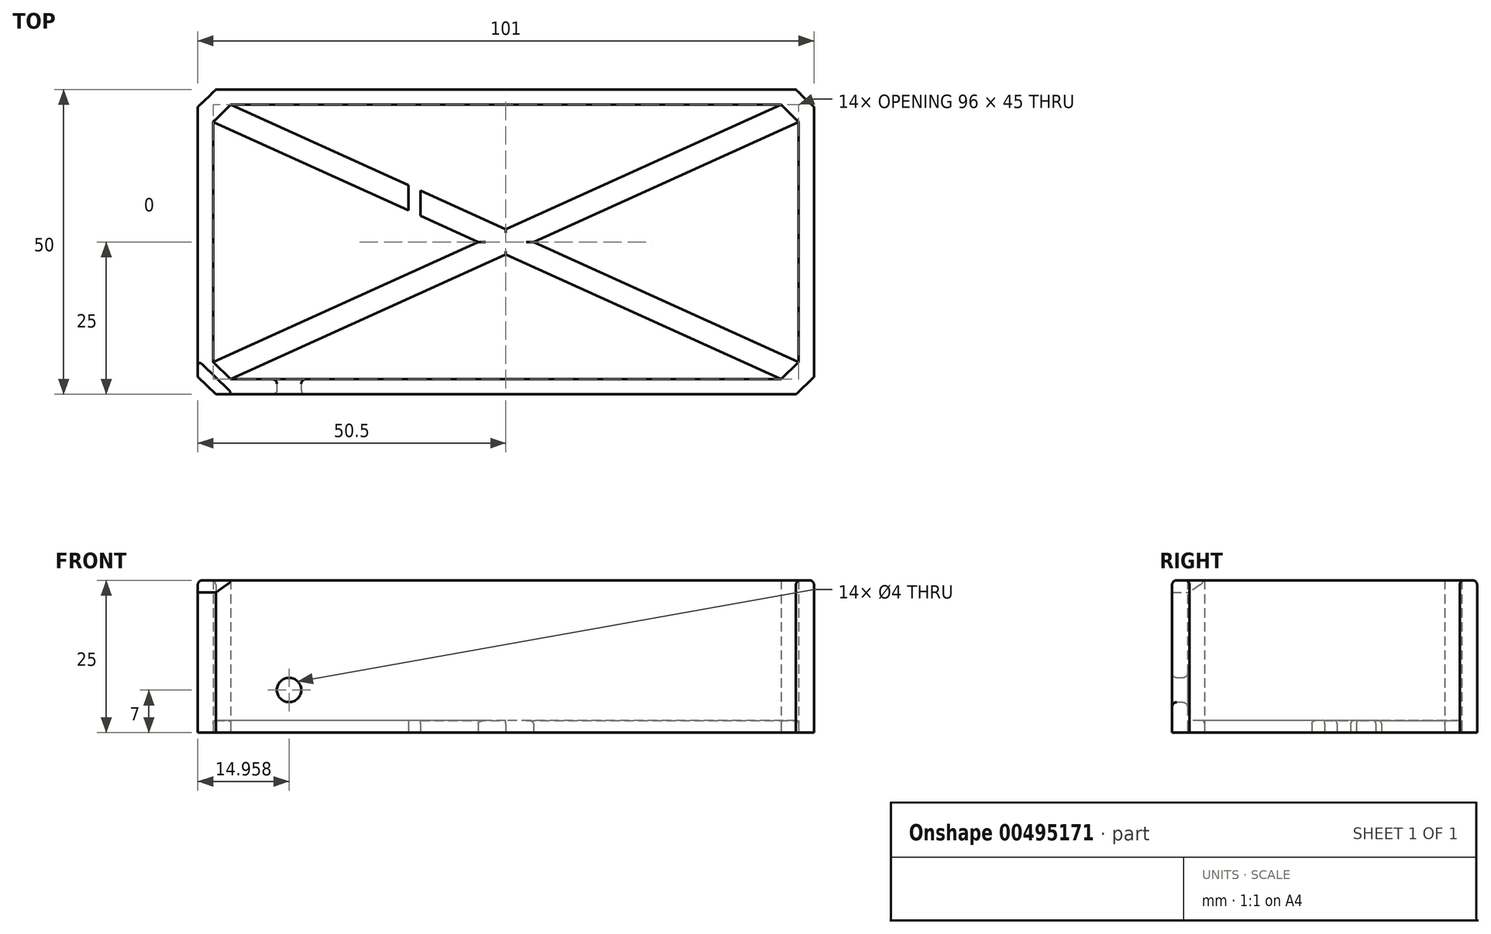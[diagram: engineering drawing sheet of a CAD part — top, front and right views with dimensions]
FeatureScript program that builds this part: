
annotation { "Feature Type Name" : "Feature", "Feature Type Description" : "" }
export const myFeature = defineFeature(function(context is Context, id is Id, definition is map)
    precondition{}
    {
        {
            var Q0;
            Q0=qCreatedBy(makeId("Top.planeOp"),FACE);
            var sketch = newSketch(context, id + "F0", { "sketchPlane" : qUnion([Q0])});
            skLineSegment(sketch, "E0.bottom", {"start": v(-47.54, 25) * mm, "end": v(47.54, 25) * mm});
            skLineSegment(sketch, "E0.top", {"start": v(-47.54, -25) * mm, "end": v(47.54, -25) * mm});
            skLineSegment(sketch, "E0.left", {"start": v(-50.5, 22.14) * mm, "end": v(-50.5, -22.14) * mm});
            skLineSegment(sketch, "E0.right", {"start": v(50.5, 22.14) * mm, "end": v(50.5, -22.14) * mm});
            skPoint(sketch, "E0.middle", {"position": v(0, 0) * mm});
            skLineSegment(sketch, "E1", {"start": v(-47.54, 25) * mm, "end": v(-50.5, 22.14) * mm});
            skPoint(sketch, "E2.orphan", {"position": v(-50.5, 25) * mm});
            skLineSegment(sketch, "E3.MirrorCS", {"start": v(-47.54, -25) * mm, "end": v(-50.5, -22.14) * mm});
            skLineSegment(sketch, "E4.MirrorCS", {"start": v(47.54, 25) * mm, "end": v(50.5, 22.14) * mm});
            skLineSegment(sketch, "E5.MirrorCS", {"start": v(47.54, -25) * mm, "end": v(50.5, -22.14) * mm});
            skPoint(sketch, "E6.orphan", {"position": v(50.5, 25) * mm});
            skPoint(sketch, "E7.orphan", {"position": v(50.5, -25) * mm});
            skPoint(sketch, "E8.orphan", {"position": v(-50.5, -25) * mm});
            skLineSegment(sketch, "E9.bottom", {"start": v(-45.1, 22.5) * mm, "end": v(45.1, 22.5) * mm});
            skLineSegment(sketch, "E9.top", {"start": v(-45.1, -22.5) * mm, "end": v(45.1, -22.5) * mm});
            skLineSegment(sketch, "E9.left", {"start": v(-48, 19.7) * mm, "end": v(-48, -19.7) * mm});
            skLineSegment(sketch, "E9.right", {"start": v(48, 19.7) * mm, "end": v(48, -19.7) * mm});
            skLineSegment(sketch, "E10", {"start": v(-48, -19.7) * mm, "end": v(-45.1, -22.5) * mm});
            skPoint(sketch, "E11.orphan", {"position": v(-48, -22.5) * mm});
            skLineSegment(sketch, "E12.MirrorCS", {"start": v(-48, 19.7) * mm, "end": v(-45.1, 22.5) * mm});
            skPoint(sketch, "E13.orphan", {"position": v(-48, 22.5) * mm});
            skLineSegment(sketch, "E14.MirrorCS", {"start": v(48, 19.7) * mm, "end": v(45.1, 22.5) * mm});
            skLineSegment(sketch, "E15.MirrorCS", {"start": v(48, -19.7) * mm, "end": v(45.1, -22.5) * mm});
            skPoint(sketch, "E16.orphan", {"position": v(48, 22.5) * mm});
            skPoint(sketch, "E17.orphan", {"position": v(48, -22.5) * mm});
            skLineSegment(sketch, "E18", {"start": v(-14, 8.4) * mm, "end": v(0, 2.06) * mm});
            skLineSegment(sketch, "E19", {"start": v(45.1, -22.5) * mm, "end": v(0, -2.06) * mm});
            skLineSegment(sketch, "E20", {"start": v(45.1, 22.5) * mm, "end": v(0, 2.06) * mm});
            skLineSegment(sketch, "E21", {"start": v(48, 19.7) * mm, "end": v(4.55, 0) * mm});
            skLineSegment(sketch, "E22.trimOffspring", {"start": v(-4.55, 0) * mm, "end": v(-14, 4.28) * mm});
            skLineSegment(sketch, "E23.trimOffspring", {"start": v(-4.55, 0) * mm, "end": v(-48, -19.7) * mm});
            skLineSegment(sketch, "E24.trimOffspring", {"start": v(4.55, 0) * mm, "end": v(48, -19.7) * mm});
            skLineSegment(sketch, "E25.trimOffspring", {"start": v(0, -2.06) * mm, "end": v(-45.1, -22.5) * mm});
            skLineSegment(sketch, "E26.bottom", {"start": v(-45.1, 22.5) * mm, "end": v(-14, 22.5) * mm});
            skLineSegment(sketch, "E26.top", {"start": v(-48, 1.5) * mm, "end": v(-14, 1.5) * mm});
            skLineSegment(sketch, "E26.left", {"start": v(-48, 19.7) * mm, "end": v(-48, 1.5) * mm});
            skLineSegment(sketch, "E26.right", {"start": v(-14, 22.5) * mm, "end": v(-14, 8.4) * mm});
            skLineSegment(sketch, "E27", {"start": v(-16, 5.19) * mm, "end": v(-48, 19.7) * mm});
            skLineSegment(sketch, "E28", {"start": v(-16, 9.31) * mm, "end": v(-45.1, 22.5) * mm});
            skLineSegment(sketch, "E29.bottom", {"start": v(-45.1, 22.5) * mm, "end": v(-16, 22.5) * mm});
            skLineSegment(sketch, "E29.top", {"start": v(-48, 3.5) * mm, "end": v(-16, 3.5) * mm});
            skLineSegment(sketch, "E29.left", {"start": v(-48, 19.7) * mm, "end": v(-48, 3.5) * mm});
            skLineSegment(sketch, "E29.right", {"start": v(-16, 22.5) * mm, "end": v(-16, 9.31) * mm});
            skLineSegment(sketch, "E30.trimOffspring", {"start": v(-16, 5.19) * mm, "end": v(-16, 3.5) * mm});
            skLineSegment(sketch, "E31.trimOffspring", {"start": v(-14, 4.28) * mm, "end": v(-14, 1.5) * mm});
            skLineSegment(sketch, "E32", {"start": v(-16, 9.31) * mm, "end": v(-16, 5.19) * mm});
            skLineSegment(sketch, "E33", {"start": v(-14, 8.4) * mm, "end": v(-14, 4.28) * mm});
            skSolve(sketch);
        }
        {
            var Q0;
            Q0=makeQuery(id+"F0.imprint","IMPRINT",FACE,{"disambiguationData":[TD([[makeQuery(id+"F0.imprint","IMPRINT",EDGE,{"derivedFrom":sQuery(id+"F0.wireOp",EDGE,"E0.bottom")}),-1.0]])]});
            extrude(context, id + "F1", {"entities" : qUnion([Q0]), "depth" : 25 * mm});
        }
        {
            var Q0;
            Q0=makeQuery(id+"F1.opExtrude","SWEPT_FACE",FACE,{"disambiguationData":[OSD([sQuery(id+"F0.wireOp",EDGE,"E0.top")])]});
            var sketch = newSketch(context, id + "F2", { "sketchPlane" : qUnion([Q0])});
            skCircle(sketch, "E34", {"center": v(-35.54, 7) * mm, "radius": 2 * mm});
            skPoint(sketch, "E34.first.point", {"position": v(-37.5, 7.44) * mm});
            skPoint(sketch, "E34.second.point", {"position": v(-33.55, 6.79) * mm});
            skPoint(sketch, "E34.third.point", {"position": v(-36.16, 5.1) * mm});
            skSolve(sketch);
        }
        {
            var Q0;
            Q0=makeQuery(id+"F2.imprint","IMPRINT",FACE,{"disambiguationData":[TD([[makeQuery(id+"F2.imprint","IMPRINT",EDGE,{"derivedFrom":sQuery(id+"F2.wireOp",EDGE,"E34")}),1.0]])]});
            extrude(context, id + "F3", {"entities" : qUnion([Q0]), "operationType" : NewBodyOperationType.REMOVE, "oppositeDirection" : true, "depth" : 25 * mm});
        }
        {
            var Q0;
            Q0=makeQuery(id+"F1.opExtrude","CAP_EDGE",EDGE,{"disambiguationData":[OSD([sQuery(id+"F0.wireOp",EDGE,"E3.MirrorCS")])],"isStart":false});
            var Q1;
            Q1=makeQuery(id+"F1.opExtrude","CAP_EDGE",EDGE,{"disambiguationData":[OSD([sQuery(id+"F0.wireOp",EDGE,"E5.MirrorCS")])],"isStart":false});
            var Q2;
            Q2=makeQuery(id+"F1.opExtrude","CAP_EDGE",EDGE,{"disambiguationData":[OSD([sQuery(id+"F0.wireOp",EDGE,"E4.MirrorCS")])],"isStart":false});
            var Q3;
            Q3=makeQuery(id+"F1.opExtrude","CAP_EDGE",EDGE,{"disambiguationData":[OSD([sQuery(id+"F0.wireOp",EDGE,"E1")])],"isStart":false});
            chamfer(context, id + "F4", {"entities" : qUnion([Q0, Q1, Q2, Q3]), "width" : 2 * mm, "tangentPropagation" : true});
        }
        {
            var Q0;
            Q0=makeQuery(id+"F0.imprint","IMPRINT",FACE,{"disambiguationData":[TD([[makeQuery(id+"F0.imprint","IMPRINT",EDGE,{"derivedFrom":sQuery(id+"F0.wireOp",EDGE,"E12.MirrorCS")}),-1.0]])]});
            var Q1;
            Q1=makeQuery(id+"F0.imprint","IMPRINT",FACE,{"disambiguationData":[TD([[makeQuery(id+"F0.imprint","IMPRINT",EDGE,{"derivedFrom":sQuery(id+"F0.wireOp",EDGE,"E26.bottom")}),-1.0]])]});
            var Q2;
            Q2=makeQuery(id+"F0.imprint","IMPRINT",FACE,{"disambiguationData":[TD([[makeQuery(id+"F0.imprint","IMPRINT",EDGE,{"derivedFrom":sQuery(id+"F0.wireOp",EDGE,"E10")}),1.0]])]});
            extrude(context, id + "F5", {"entities" : qUnion([Q0, Q1, Q2]), "depth" : 2 * mm});
        }
        {
            var Q0;
            Q0=makeQuery(id+"F5.opExtrude","CAP_EDGE",EDGE,{"disambiguationData":[OSD([sQuery(id+"F0.wireOp",EDGE,"E28")])],"isStart":false});
            var Q1;
            Q1=makeQuery(id+"F5.opExtrude","CAP_EDGE",EDGE,{"disambiguationData":[OSD([sQuery(id+"F0.wireOp",EDGE,"E27")])],"isStart":false});
            var Q2;
            Q2=makeQuery(id+"F5.opExtrude","CAP_EDGE",EDGE,{"disambiguationData":[OSD([sQuery(id+"F0.wireOp",EDGE,"E29.top")])],"isStart":false});
            var Q3;
            Q3=makeQuery(id+"F5.opExtrude","CAP_EDGE",EDGE,{"disambiguationData":[OSD([sQuery(id+"F0.wireOp",EDGE,"E26.top")])],"isStart":false});
            var Q4;
            Q4=makeQuery(id+"F5.opExtrude","CAP_EDGE",EDGE,{"disambiguationData":[OSD([sQuery(id+"F0.wireOp",EDGE,"E31.trimOffspring")])],"isStart":false});
            var Q5;
            Q5=makeQuery(id+"F5.opExtrude","CAP_EDGE",EDGE,{"disambiguationData":[OSD([sQuery(id+"F0.wireOp",EDGE,"E22.trimOffspring")])],"isStart":false});
            var Q6;
            Q6=makeQuery(id+"F5.opExtrude","CAP_EDGE",EDGE,{"disambiguationData":[OSD([sQuery(id+"F0.wireOp",EDGE,"E20")])],"isStart":false});
            var Q7;
            Q7=makeQuery(id+"F5.opExtrude","CAP_EDGE",EDGE,{"disambiguationData":[OSD([sQuery(id+"F0.wireOp",EDGE,"E21")])],"isStart":false});
            var Q8;
            Q8=makeQuery(id+"F5.opExtrude","CAP_EDGE",EDGE,{"disambiguationData":[OSD([sQuery(id+"F0.wireOp",EDGE,"E19")])],"isStart":false});
            var Q9;
            Q9=makeQuery(id+"F5.opExtrude","CAP_EDGE",EDGE,{"disambiguationData":[OSD([sQuery(id+"F0.wireOp",EDGE,"E24.trimOffspring")])],"isStart":false});
            var Q10;
            Q10=makeQuery(id+"F5.opExtrude","CAP_EDGE",EDGE,{"disambiguationData":[OSD([sQuery(id+"F0.wireOp",EDGE,"E25.trimOffspring")])],"isStart":false});
            var Q11;
            Q11=makeQuery(id+"F5.opExtrude","CAP_EDGE",EDGE,{"disambiguationData":[OSD([sQuery(id+"F0.wireOp",EDGE,"E23.trimOffspring")])],"isStart":false});
            var Q12;
            Q12=makeQuery(id+"F5.opExtrude","CAP_EDGE",EDGE,{"disambiguationData":[OSD([sQuery(id+"F0.wireOp",EDGE,"E26.right")])],"isStart":false});
            var Q13;
            Q13=makeQuery(id+"F5.opExtrude","CAP_EDGE",EDGE,{"disambiguationData":[OSD([sQuery(id+"F0.wireOp",EDGE,"E29.right")])],"isStart":false});
            var Q14;
            Q14=makeQuery(id+"F5.opExtrude","CAP_EDGE",EDGE,{"disambiguationData":[OSD([sQuery(id+"F0.wireOp",EDGE,"E18")])],"isStart":false});
            fillet(context, id + "F6", {"entities" : qUnion([Q0, Q1, Q2, Q3, Q4, Q5, Q6, Q7, Q8, Q9, Q10, Q11, Q12, Q13, Q14]), "radius" : .5 * mm, "tangentPropagation" : true, "allowEdgeOverflow" : false});
        }
        {
            var Q0;
            Q0=makeQuery(id+"F1.opExtrude","CAP_EDGE",EDGE,{"disambiguationData":[OSD([sQuery(id+"F0.wireOp",EDGE,"E0.top")])],"isStart":false});
            var Q1;
            Q1=makeQuery(id+"F1.opExtrude","CAP_EDGE",EDGE,{"disambiguationData":[OSD([sQuery(id+"F0.wireOp",EDGE,"E0.left")])],"isStart":false});
            var Q2;
            Q2=makeQuery(id+"F1.opExtrude","CAP_EDGE",EDGE,{"disambiguationData":[OSD([sQuery(id+"F0.wireOp",EDGE,"E0.bottom")])],"isStart":false});
            var Q3;
            Q3=makeQuery(id+"F1.opExtrude","CAP_EDGE",EDGE,{"disambiguationData":[OSD([sQuery(id+"F0.wireOp",EDGE,"E0.right")])],"isStart":false});
            var Q4;
            Q4=makeQuery(id+"F3.boolean.opBoolean","COPY",FACE,{"derivedFrom":makeQuery(id+"F3.opExtrude","SWEPT_FACE",FACE,{"disambiguationData":[OSD([sQuery(id+"F2.wireOp",EDGE,"E34")])]})});
            var Q5;
            Q5=makeQuery(id+"FdQ0bMW0v6bhTqe_1.opExtrude","CAP_EDGE",EDGE,{"disambiguationData":[OSD([sQuery(id+"F0.wireOp",EDGE,"E22.trimOffspring")])],"isStart":false});
            var Q6;
            Q6=makeQuery(id+"FdQ0bMW0v6bhTqe_1.opExtrude","CAP_EDGE",EDGE,{"disambiguationData":[OSD([sQuery(id+"F0.wireOp",EDGE,"E18")])],"isStart":false});
            var Q7;
            Q7=makeQuery(id+"FdQ0bMW0v6bhTqe_1.opExtrude","CAP_EDGE",EDGE,{"disambiguationData":[OSD([sQuery(id+"F0.wireOp",EDGE,"E20")])],"isStart":false});
            var Q8;
            Q8=makeQuery(id+"FdQ0bMW0v6bhTqe_1.opExtrude","CAP_EDGE",EDGE,{"disambiguationData":[OSD([sQuery(id+"F0.wireOp",EDGE,"E25.trimOffspring")])],"isStart":false});
            var Q9;
            Q9=makeQuery(id+"FdQ0bMW0v6bhTqe_1.opExtrude","CAP_EDGE",EDGE,{"disambiguationData":[OSD([sQuery(id+"F0.wireOp",EDGE,"E23.trimOffspring")])],"isStart":false});
            var Q10;
            Q10=makeQuery(id+"FdQ0bMW0v6bhTqe_1.opExtrude","CAP_EDGE",EDGE,{"disambiguationData":[OSD([sQuery(id+"F0.wireOp",EDGE,"E19")])],"isStart":false});
            var Q11;
            Q11=makeQuery(id+"FdQ0bMW0v6bhTqe_1.opExtrude","CAP_EDGE",EDGE,{"disambiguationData":[OSD([sQuery(id+"F0.wireOp",EDGE,"E24.trimOffspring")])],"isStart":false});
            var Q12;
            Q12=makeQuery(id+"FdQ0bMW0v6bhTqe_1.opExtrude","CAP_EDGE",EDGE,{"disambiguationData":[OSD([sQuery(id+"F0.wireOp",EDGE,"E21")])],"isStart":false});
            fillet(context, id + "F7", {"entities" : qUnion([Q0, Q1, Q2, Q3, Q4, Q5, Q6, Q7, Q8, Q9, Q10, Q11, Q12]), "radius" : .75 * mm, "tangentPropagation" : true, "allowEdgeOverflow" : false});
        }
    });
